# Revit family: Grundplatten Typ   I, V2A
name_source: partatom
category: HLS-Bauteile
revit_build: Autodesk Revit 2017 (Build: 20190507_1515(x64)
units: mm (PartAtom-declared; Revit-internal decimal feet)

## family parameters
Arbeitsebenenbasiert = Ja
Beim Laden mit Abzugskörper schneiden = Nein
Bemaßung runder Anschluss = Durchmesser verwenden
Gemeinsam genutzt = Ja
Immer vertikal = Nein
Raumberechnungspunkt = Nein
Teiletyp = Normal

## types (5) — shared parameters
Abmessung = 115 x 35 x 4 mm
Anzahl Befestigungsloch = 2
B = 35 mm  [stored 0.114829 ft]
Breite = 35 mm  [stored 0.114829 ft]
D = 13 mm  [stored 0.0426509 ft]
Fabrikat = MEFA
Firma = MEFA Befestigungs- und Montagesysteme GmbH
Kurztext1 = Grundplatte Typ I V2A
L = 115 mm  [stored 0.377297 ft]
L1 = 85 mm  [stored 0.278871 ft]
Lochabstand längs = 85 mm  [stored 0.278871 ft]
Lochdurchmesser = 13 mm
Länge = 115 mm  [stored 0.377297 ft]
MD = 4 mm  [stored 0.0131234 ft]
Material = Edelstahl
Materialname = V2A
Mengeneinheit = St
Oberflaeche = Edelstahl
Stärke = 4 mm  [stored 0.0131234 ft]
Vorgabe-Ansicht = 1219 mm
max. zul. Last hängend = 1.35 kN
vpe = 1 St
zero-valued in all types: Sicherheitsfaktor

## per-type parameters (varying)
| type | Anschluss | Artikelnummer | Gewicht | Gewicht pro Bauteil | Gewindeanschluss | H | HGA | Kurztext2 |
| Grundplatte Typ I, 115x35x 4, M 8, V2A | M8 | 0599479 | 0.13 kg | 0.13 kg | 6kt-Mutter parametrik : A4 Mutter M8 | 11 mm | 7 mm  [stored 0.0229659 ft] | Anschluss M8 Platte 115x35x4 mm |
| Grundplatte Typ I, 115x35x 4, M10, V2A | M10 | 0599495 | 0.13 kg | 0.13 kg | 6kt-Mutter parametrik : A4 Mutter M10 | 12 mm  [stored 0.0393701 ft] | 8 mm  [stored 0.0262467 ft] | Anschluss M10 Platte 115x35x4 mm |
| Grundplatte Typ I, 115x35x 4, M12, V2A | M12 | 0599061 | 0.14 kg | 0.14 kg | 6kt-Mutter parametrik : A4 Mutter M12 | 14 mm  [stored 0.0459318 ft] | 10 mm  [stored 0.0328084 ft] | Anschluss M12 Platte 115x35x4 mm |
| Grundplatte Typ I, 115x35x 4, M16, V2A | M16 | 0599088 | 0.16 kg | 0.16 kg | 6kt-Mutter parametrik : A4 Mutter M16 | 17 mm | 13 mm  [stored 0.0426509 ft] | Anschluss M16 Platte 115x35x4 mm |
| Grundplatte Typ I, 115x35x 4, 1/2", V2A | 1/2'' | 0599045 | 0.15 kg | 0.15 kg | Runde Gewindeanschlusse parametrik : Muffe 1/2´´ (0009865) | 19 mm  [stored 0.062336 ft] | 15 mm  [stored 0.0492126 ft] | Anschluss 1/2'' Platte 115x35x4 mm |

note: [stored X ft] marks values corroborated as IEEE doubles in the binary element streams (Revit-internal decimal feet)

## geometry (parser evidence)
native form markers: Sweep x6
no freeform markers — native parametric forms only
